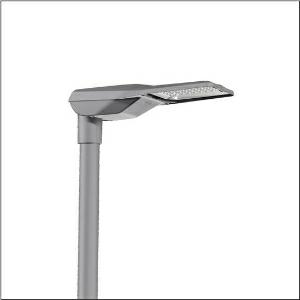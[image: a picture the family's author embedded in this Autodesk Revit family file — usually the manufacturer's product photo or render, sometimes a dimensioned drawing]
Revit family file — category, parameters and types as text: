
# Revit family: streetlight_sl_21_iq_mini___p1_0a_5xe2a31d08hb_09ea
name_source: partatom
category: Lighting Fixtures
units: mm (PartAtom-declared; Revit-internal decimal feet)

## family parameters
Cut with Voids When Loaded = No
Host = Face
Light Source = No
Part Type = Normal
Room Calculation Point = No
Round Connector Dimension = Use Diameter
Shared = No

## types (1)
- --- (1 x LED, 9450 lm, 70.9 W, 3000K)
    Apparent Load = 71 VA
    CIE Flux Codes = 21 50 90 100 100
    Color Rendering = 70
    Color Temperature = 3000K
    Default Elevation = 1800 mm
    Description = Streetlight SL 21 iQ mini, mast luminaire, primary light control with lens, of PMMA, primary optical cover: cover, of toughened safety glass, transparent, light distribution: P1.0a, light emission: direct distribution, primary light characteristic: asymmetric, installation type: post-top, side-entry, LED, High Power LED, rated luminous flux: 9.450lm, luminous efficacy: 133lm/W, light colour: 730, colour temperature: 3000K, control gear: iQ-Comfort, control: Auto-Match, Temp-Guard, Lumen-Switch, Night-Set, Smart-Wire, Light-Fading, Desk-Remote (wireless, voltage-free reading and setting of iQ features in the workshop via application-optimized NFC function/RFID function), optimised constant luminous flux control (CLO 2.0), pre-setting: linear dimming characteristic, mains connection: 220..240V, AC, 50/60Hz, start of lifetime: 71W, end of service life: 75W, reduction: 31W, luminaire housing, of diecast aluminium, powder-coated, Siteco® metallic grey (DB 702S), corrosivity category C5 mid according to DIN EN ISO 12944, please order mast flange separately, inclination adjustable: 0°, 5°, 10°, 15°, sealing non-destructively replaceable, multi-level sealing system, length: 628mm, width: 235mm, height: 110mm, mast flange for spigot size: 42mm (side-entry): 5XC10008XM4, 60/48mm (side-entry/post-top): 5XC10108XM2, 76/60mm (side-entry/post-top): 5XC10108XM1, mounting height: 4..8m, protection rating (complete): IP66, insulation class (complete): insulation class II (safety insulation), certification: CE, ENEC, ENEC+, VDE, impact resistance: IK10, permissible operating ambient temperature for outdoor applications: -40..+50°C, standard-compliant lighting for roads and squares, packaging unit: 1 piece

Light Distribution: P1.0a
    Height = 110 mm
    Lamp = 1 x LED
    Lamp Light Flux = 9450 lm
    Lamp Power = 70.9 W
    Lamp count = 1
    Length = 625 mm
    Luminous efficacy = 133 lm/W
    Manufacturer = Siteco
    ModVariant = No
    Model = 5XE2A31D08HB
    Number of Poles = 1
    OnlyDefault = Yes
    Power Factor = 1
    Product Name = Streetlight SL 21 iQ mini | P1.0a
    Product group = mast luminaire | pylon top
    ProductGroupID = 6100
    Protection Class = Protection class II
    Protection Degree = IP 66
    RLX_Detail_Level = 1
    RLX_Emergency_Light_Flux = 0 lm
    RLX_Emergency_Type = 0
    RLX_Emergency_Type_DB = No
    RlxData = <blob elided: 37617 chars, md5=3cb55bf3>
    Socket = socket
    Standby Power = 0 W
    System Light Flux = 9450 lm
    System Power = 71 W
    Type Comments = factory setting: luminous flux: 100 % | dim-lin: 254 | 711 mA
    Type Image = l_1003519.jpg
    URL = http://relux.com
    VarID = @adj_179173
    Voltage = 0 V
    Weight = 0.00 kg
    Width = 234 mm

## geometry (parser evidence)
native form markers: Blend x4, Sweep x10
no freeform markers — native parametric forms only
